# Revit family: Haworth_Poppy_Chair_Guest_AP_PRELIMINARY
name_source: partatom
category: Furniture
units: mm (PartAtom-declared; Revit-internal decimal feet)

## family parameters
Always vertical = Yes
Cut with Voids When Loaded = No
OmniClass Number = 23.40.70.14.64.11
OmniClass Title = Office Furniture
Room Calculation Point = No
Shared = No
Work Plane-Based = No

## types (3) — shared parameters
Actual Depth = 584 mm
Actual Height = 835 mm
Actual Width = 686 mm
Arm Support Finish = Haworth _ Paint _ Black
Assembly Code = E2020200
Description = Haworth - Poppy - Guest - Chair
Manufacturer = Haworth
Model = SEPOX
Product URL = https://www.haworth.com
Revision Number = 2
Size = Verify Final Dim.w/ Haworth
URL = https://www.haworth.com
Warranty = http://www.haworth.com

## per-type parameters (varying)
| type | Wood Base |
| Four Star Base | No |
| Five Star Base | No |
| Wood Base | Yes |

type visibility flags (boolean, named after types; folded from table):
- Four Star Base: Yes: Four Star Base
- Five Star Base: Yes: Five Star Base
- Wood Base: Yes: (none)

## geometry (parser evidence)
native form markers: Sweep x14
no freeform markers — native parametric forms only
